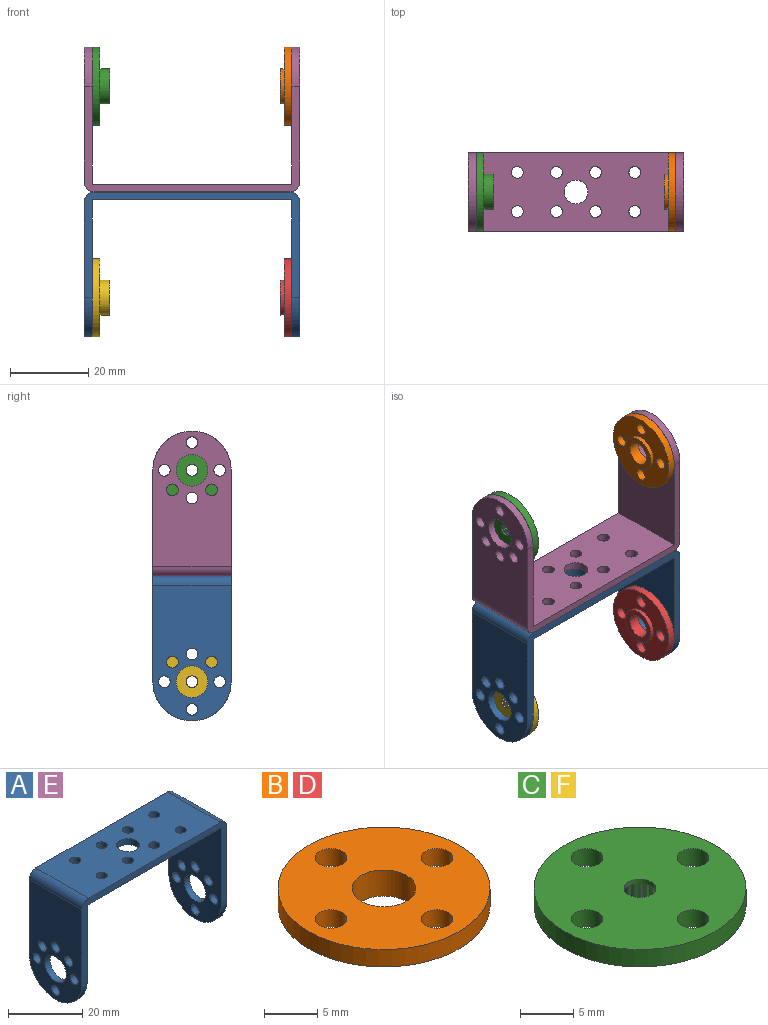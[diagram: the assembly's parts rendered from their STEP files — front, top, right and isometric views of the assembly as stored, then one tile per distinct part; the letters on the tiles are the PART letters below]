
ASSEMBLY  parts=6 mates=5
PART A: 35 faces, bbox 55x20x37 mm
  f0: plane 55x27mm, normal (0,1,0), area 207.3mm2, adj f2,f3,f4,f5,f6,f7,f8,f9
  f1: plane 55x27mm, normal (0,-1,0), area 207.3mm2, adj f2,f3,f4,f5,f6,f7,f8,f9
  f2: plane 35x20mm, normal (-1,0,0), area 563.1mm2, adj f0,f1,f3,f9,f16,f23,f24,f25
  f3: plane 51x20mm, normal (0,0,-1), area 934.2mm2, adj f0,f1,f2,f4,f10,f11,f12,f13
  f4: plane 35x20mm, normal (1,0,0), area 563.1mm2, adj f0,f1,f3,f8,f15,f17,f18,f19
  f5: plane 34.5x20mm, normal (1,0,0), area 553.1mm2, adj f0,f1,f9,f16,f23,f24,f25,f26
  f6: plane 50x20mm, normal (0,0,1), area 914.2mm2, adj f0,f1,f10,f11,f12,f13,f14,f29
  f7: plane 34.5x20mm, normal (-1,0,0), area 553.1mm2, adj f0,f1,f8,f15,f17,f18,f19,f20
  f8: cylinder r=10mm len=20mm, axis (-1,0,0), area 62.8mm2, adj f0,f1,f4,f7
  f9: cylinder r=10mm len=20mm, axis (1,0,0), area 62.8mm2, adj f0,f1,f2,f5
  f10: cylinder r=3.05mm len=6.1mm, axis (0,0,-1), area 38.3mm2, adj f3,f6
  f11: cylinder r=1.5mm len=3mm, axis (0,0,-1), area 18.8mm2, adj f3,f6
  f12: cylinder r=1.5mm len=3mm, axis (0,0,-1), area 18.8mm2, adj f3,f6
  f13: cylinder r=1.5mm len=3mm, axis (0,0,-1), area 18.8mm2, adj f3,f6
  f14: cylinder r=1.5mm len=3mm, axis (0,0,-1), area 18.8mm2, adj f3,f6
  f15: cylinder r=4.05mm len=8.1mm, axis (1,0,0), area 50.9mm2, adj f4,f7
  f16: cylinder r=4.05mm len=8.1mm, axis (1,0,0), area 50.9mm2, adj f2,f5
  f17: cylinder r=1.5mm len=3mm, axis (1,0,0), area 18.8mm2, adj f4,f7
  f18: cylinder r=1.5mm len=3mm, axis (1,0,0), area 18.8mm2, adj f4,f7
  f19: cylinder r=1.5mm len=3mm, axis (1,0,0), area 18.8mm2, adj f4,f7
  f20: cylinder r=1.5mm len=3mm, axis (1,0,0), area 18.8mm2, adj f4,f7
  f21: cylinder r=1.5mm len=3mm, axis (1,0,0), area 18.8mm2, adj f4,f7
  f22: cylinder r=1.5mm len=3mm, axis (1,0,0), area 18.8mm2, adj f4,f7
  f23: cylinder r=1.5mm len=3mm, axis (1,0,0), area 18.8mm2, adj f2,f5
  f24: cylinder r=1.5mm len=3mm, axis (1,0,0), area 18.8mm2, adj f2,f5
  f25: cylinder r=1.5mm len=3mm, axis (1,0,0), area 18.8mm2, adj f2,f5
  f26: cylinder r=1.5mm len=3mm, axis (1,0,0), area 18.8mm2, adj f2,f5
  f27: cylinder r=1.5mm len=3mm, axis (1,0,0), area 18.8mm2, adj f2,f5
  f28: cylinder r=1.5mm len=3mm, axis (1,0,0), area 18.8mm2, adj f2,f5
  f29: cylinder r=2.5mm len=20mm, axis (0,-1,0), area 78.5mm2, adj f0,f1,f5,f6
  f30: cylinder r=2.5mm len=20mm, axis (0,-1,0), area 78.5mm2, adj f0,f1,f6,f7
  f31: cylinder r=1.5mm len=3mm, axis (0,0,-1), area 18.8mm2, adj f3,f6
  f32: cylinder r=1.5mm len=3mm, axis (0,0,-1), area 18.8mm2, adj f3,f6
  f33: cylinder r=1.5mm len=3mm, axis (0,0,-1), area 18.8mm2, adj f3,f6
  f34: cylinder r=1.5mm len=3mm, axis (0,0,-1), area 18.8mm2, adj f3,f6
PART B: 10 faces, bbox 20x20x3 mm
  f0: cylinder r=4.5mm len=9mm, axis (0,0,-1), area 28.3mm2, adj f1,f5
  f1: plane 9x9mm, normal (0,0,-1), area 35.3mm2, adj f0,f2
  f2: cylinder r=3mm len=6mm, axis (0,0,-1), area 56.5mm2, adj f1,f3
  f3: plane 20x20mm, normal (0,0,1), area 257.6mm2, adj f2,f4,f6,f7,f8,f9
  f4: cylinder r=10mm len=20mm, axis (0,0,-1), area 125.7mm2, adj f3,f5
  f5: plane 20x20mm, normal (0,0,-1), area 222.3mm2, adj f0,f4,f6,f7,f8,f9
  f6: cylinder r=1.5mm len=3mm, axis (0,0,-1), area 18.8mm2, adj f3,f5
  f7: cylinder r=1.5mm len=3mm, axis (0,0,-1), area 18.8mm2, adj f3,f5
  f8: cylinder r=1.5mm len=3mm, axis (0,0,-1), area 18.8mm2, adj f3,f5
  f9: cylinder r=1.5mm len=3mm, axis (0,0,-1), area 18.8mm2, adj f3,f5
PART C: 152 faces, bbox 20x20x4.5 mm
  f0: plane 20x20mm, normal (0,0,1), area 278.8mm2, adj f1,f5,f6,f7,f8,f11
  f1: cylinder r=10mm len=20mm, axis (0,0,-1), area 125.7mm2, adj f0,f2
  f2: plane 20x20mm, normal (0,0,-1), area 222.3mm2, adj f1,f3,f5,f6,f7,f8
  f3: cylinder r=4.5mm len=9mm, axis (0,0,-1), area 70.7mm2, adj f2,f4
  f4: plane 9x9mm, normal (0,0,-1), area 35.3mm2, adj f3,f10,f15,f18,f21,f24,f27,f30
  f5: cylinder r=1.5mm len=3mm, axis (0,0,-1), area 18.8mm2, adj f0,f2
  f6: cylinder r=1.5mm len=3mm, axis (0,0,-1), area 18.8mm2, adj f0,f2
  f7: cylinder r=1.5mm len=3mm, axis (0,0,-1), area 18.8mm2, adj f0,f2
  f8: cylinder r=1.5mm len=3mm, axis (0,0,-1), area 18.8mm2, adj f0,f2
  f9: cone r=3mm half-angle=45deg, axis (0,0,-1), area 12.1mm2, adj f10,f12,f13,f14,f15,f16,f17,f18
  f10: cylinder r=3mm len=3.35mm, axis (0,0,-1), area 1mm2, adj f4,f9,f13,f14
  f11: cylinder r=1.5mm len=3mm, axis (0,0,-1), area 4.7mm2, adj f0,f12
  f12: plane 4.7x4.7mm, normal (0,0,-1), area 10.3mm2, adj f9,f11
  f13: plane 3.76x0.42mm, normal (0.23,0.97,0), area 1.4mm2, adj f9,f10,f96,f97
  f14: plane 3.76x0.42mm, normal (0.23,-0.97,0), area 1.4mm2, adj f9,f10,f150,f151
  f15: cylinder r=3mm len=3.35mm, axis (0,0,-1), area 1mm2, adj f4,f9,f16,f17
  f16: plane 3.76x0.39mm, normal (0.45,0.9,0), area 1.4mm2, adj f9,f15,f150,f151
  f17: plane 3.76x0.43mm, normal (0.01,-1,0), area 1.4mm2, adj f9,f15,f148,f149
  f18: cylinder r=3mm len=3.35mm, axis (0,0,-1), area 1mm2, adj f4,f9,f19,f20
  f19: plane 3.76x0.33mm, normal (0.63,0.77,0), area 1.4mm2, adj f9,f18,f148,f149
  f20: plane 3.76x0.42mm, normal (-0.21,-0.98,0), area 1.4mm2, adj f9,f18,f146,f147
  f21: cylinder r=3mm len=3.35mm, axis (0,0,-1), area 1mm2, adj f4,f9,f22,f23
  f22: plane 3.76x0.34mm, normal (0.79,0.61,0), area 1.4mm2, adj f9,f21,f146,f147
  f23: plane 3.76x0.39mm, normal (-0.42,-0.91,0), area 1.4mm2, adj f9,f21,f144,f145
  f24: cylinder r=3mm len=3.35mm, axis (0,0,-1), area 1mm2, adj f4,f9,f25,f26
  f25: plane 3.76x0.39mm, normal (0.91,0.42,0), area 1.4mm2, adj f9,f24,f144,f145
  f26: plane 3.76x0.34mm, normal (-0.61,-0.79,0), area 1.4mm2, adj f9,f24,f142,f143
  f27: cylinder r=3mm len=3.35mm, axis (0,0,-1), area 1mm2, adj f4,f9,f28,f29
  f28: plane 3.76x0.42mm, normal (0.98,0.21,0), area 1.4mm2, adj f9,f27,f142,f143
  f29: plane 3.76x0.33mm, normal (-0.77,-0.63,0), area 1.4mm2, adj f9,f27,f140,f141
  f30: cylinder r=3mm len=3.35mm, axis (0,0,-1), area 1mm2, adj f4,f9,f31,f32
  f31: plane 3.76x0.43mm, normal (1,-0.01,0), area 1.4mm2, adj f9,f30,f140,f141
  f32: plane 3.76x0.39mm, normal (-0.9,-0.45,0), area 1.4mm2, adj f9,f30,f138,f139
  f33: cylinder r=3mm len=3.35mm, axis (0,0,-1), area 1mm2, adj f4,f9,f34,f35
  f34: plane 3.76x0.42mm, normal (0.97,-0.23,0), area 1.4mm2, adj f9,f33,f138,f139
  f35: plane 3.76x0.42mm, normal (-0.97,-0.23,0), area 1.4mm2, adj f9,f33,f136,f137
  f36: cylinder r=3mm len=3.35mm, axis (0,0,-1), area 1mm2, adj f4,f9,f37,f38
  f37: plane 3.76x0.39mm, normal (0.9,-0.45,0), area 1.4mm2, adj f9,f36,f136,f137
  f38: plane 3.76x0.43mm, normal (-1,-0.01,0), area 1.4mm2, adj f9,f36,f134,f135
  f39: cylinder r=3mm len=3.35mm, axis (0,0,-1), area 1mm2, adj f4,f9,f40,f41
  f40: plane 3.76x0.33mm, normal (0.77,-0.63,0), area 1.4mm2, adj f9,f39,f134,f135
  f41: plane 3.76x0.42mm, normal (-0.98,0.21,0), area 1.4mm2, adj f9,f39,f132,f133
  f42: cylinder r=3mm len=3.35mm, axis (0,0,-1), area 1mm2, adj f4,f9,f43,f44
  f43: plane 3.76x0.34mm, normal (0.61,-0.79,0), area 1.4mm2, adj f9,f42,f132,f133
  f44: plane 3.76x0.39mm, normal (-0.91,0.42,0), area 1.4mm2, adj f9,f42,f130,f131
  f45: cylinder r=3mm len=3.35mm, axis (0,0,-1), area 1mm2, adj f4,f9,f46,f47
  f46: plane 3.76x0.39mm, normal (0.42,-0.91,0), area 1.4mm2, adj f9,f45,f130,f131
  f47: plane 3.76x0.34mm, normal (-0.79,0.61,0), area 1.4mm2, adj f9,f45,f128,f129
  f48: cylinder r=3mm len=3.35mm, axis (0,0,-1), area 1mm2, adj f4,f9,f49,f50
  f49: plane 3.76x0.42mm, normal (0.21,-0.98,0), area 1.4mm2, adj f9,f48,f128,f129
  f50: plane 3.76x0.33mm, normal (-0.63,0.77,0), area 1.4mm2, adj f9,f48,f126,f127
  f51: cylinder r=3mm len=3.35mm, axis (0,0,-1), area 1mm2, adj f4,f9,f52,f53
  f52: plane 3.76x0.43mm, normal (-0.01,-1,0), area 1.4mm2, adj f9,f51,f126,f127
  f53: plane 3.76x0.39mm, normal (-0.45,0.9,0), area 1.4mm2, adj f9,f51,f124,f125
  f54: cylinder r=3mm len=3.35mm, axis (0,0,-1), area 1mm2, adj f4,f9,f55,f56
  f55: plane 3.76x0.42mm, normal (-0.23,-0.97,0), area 1.4mm2, adj f9,f54,f124,f125
  f56: plane 3.76x0.42mm, normal (-0.23,0.97,0), area 1.4mm2, adj f9,f54,f122,f123
  f57: cylinder r=3mm len=3.35mm, axis (0,0,-1), area 1mm2, adj f4,f9,f58,f59
  f58: plane 3.76x0.39mm, normal (-0.45,-0.9,0), area 1.4mm2, adj f9,f57,f122,f123
  f59: plane 3.76x0.43mm, normal (-0.01,1,0), area 1.4mm2, adj f9,f57,f120,f121
  f60: cylinder r=3mm len=3.35mm, axis (0,0,-1), area 1mm2, adj f4,f9,f61,f62
  f61: plane 3.76x0.33mm, normal (-0.63,-0.77,0), area 1.4mm2, adj f9,f60,f120,f121
  f62: plane 3.76x0.42mm, normal (0.21,0.98,0), area 1.4mm2, adj f9,f60,f118,f119
  f63: cylinder r=3mm len=3.35mm, axis (0,0,-1), area 1mm2, adj f4,f9,f64,f65
  f64: plane 3.76x0.34mm, normal (-0.79,-0.61,0), area 1.4mm2, adj f9,f63,f118,f119
  f65: plane 3.76x0.39mm, normal (0.42,0.91,0), area 1.4mm2, adj f9,f63,f116,f117
  f66: cylinder r=3mm len=3.35mm, axis (0,0,-1), area 1mm2, adj f4,f9,f67,f68
  f67: plane 3.76x0.39mm, normal (-0.91,-0.42,0), area 1.4mm2, adj f9,f66,f116,f117
  f68: plane 3.76x0.34mm, normal (0.61,0.79,0), area 1.4mm2, adj f9,f66,f114,f115
  f69: cylinder r=3mm len=3.35mm, axis (0,0,-1), area 1mm2, adj f4,f9,f70,f71
  f70: plane 3.76x0.42mm, normal (-0.98,-0.21,0), area 1.4mm2, adj f9,f69,f114,f115
  f71: plane 3.76x0.33mm, normal (0.77,0.63,0), area 1.4mm2, adj f9,f69,f112,f113
  f72: cylinder r=3mm len=3.35mm, axis (0,0,-1), area 1mm2, adj f4,f9,f73,f74
  f73: plane 3.76x0.43mm, normal (-1,0.01,0), area 1.4mm2, adj f9,f72,f112,f113
  f74: plane 3.76x0.39mm, normal (0.9,0.45,0), area 1.4mm2, adj f9,f72,f110,f111
  f75: cylinder r=3mm len=3.35mm, axis (0,0,-1), area 1mm2, adj f4,f9,f76,f77
  f76: plane 3.76x0.42mm, normal (-0.97,0.23,0), area 1.4mm2, adj f9,f75,f110,f111
  f77: plane 3.76x0.42mm, normal (0.97,0.23,0), area 1.4mm2, adj f9,f75,f108,f109
  f78: cylinder r=3mm len=3.35mm, axis (0,0,-1), area 1mm2, adj f4,f9,f79,f80
  f79: plane 3.76x0.39mm, normal (-0.9,0.45,0), area 1.4mm2, adj f9,f78,f108,f109
  f80: plane 3.76x0.43mm, normal (1,0.01,0), area 1.4mm2, adj f9,f78,f106,f107
  f81: cylinder r=3mm len=3.35mm, axis (0,0,-1), area 1mm2, adj f4,f9,f82,f83
  f82: plane 3.76x0.33mm, normal (-0.77,0.63,0), area 1.4mm2, adj f9,f81,f106,f107
  f83: plane 3.76x0.42mm, normal (0.98,-0.21,0), area 1.4mm2, adj f9,f81,f104,f105
  f84: cylinder r=3mm len=3.35mm, axis (0,0,-1), area 1mm2, adj f4,f9,f85,f86
  f85: plane 3.76x0.34mm, normal (-0.61,0.79,0), area 1.4mm2, adj f9,f84,f104,f105
  f86: plane 3.76x0.39mm, normal (0.91,-0.42,0), area 1.4mm2, adj f9,f84,f102,f103
  f87: cylinder r=3mm len=3.35mm, axis (0,0,-1), area 1mm2, adj f4,f9,f88,f89
  f88: plane 3.76x0.39mm, normal (-0.42,0.91,0), area 1.4mm2, adj f9,f87,f102,f103
  f89: plane 3.76x0.34mm, normal (0.79,-0.61,0), area 1.4mm2, adj f9,f87,f100,f101
  f90: cylinder r=3mm len=3.35mm, axis (0,0,-1), area 1mm2, adj f4,f9,f91,f92
  f91: plane 3.76x0.42mm, normal (-0.21,0.98,0), area 1.4mm2, adj f9,f90,f100,f101
  f92: plane 3.76x0.33mm, normal (0.63,-0.77,0), area 1.4mm2, adj f9,f90,f98,f99
  f93: cylinder r=3mm len=3.35mm, axis (0,0,-1), area 1mm2, adj f4,f9,f94,f95
  f94: plane 3.76x0.43mm, normal (0.01,1,0), area 1.4mm2, adj f9,f93,f98,f99
  f95: plane 3.76x0.39mm, normal (0.45,-0.9,0), area 1.4mm2, adj f9,f93,f96,f97
  f96: cone r=2.6mm half-angle=60deg, axis (0,0,-1), area 0.1mm2, adj f4,f13,f95,f97
  f97: cylinder r=2.6mm len=3.52mm, axis (0,0,-1), area 0.3mm2, adj f9,f13,f95,f96
  f98: cone r=2.6mm half-angle=60deg, axis (0,0,-1), area 0.1mm2, adj f4,f92,f94,f99
  f99: cylinder r=2.6mm len=3.52mm, axis (0,0,-1), area 0.3mm2, adj f9,f92,f94,f98
  f100: cone r=2.6mm half-angle=60deg, axis (0,0,-1), area 0.1mm2, adj f4,f89,f91,f101
  f101: cylinder r=2.6mm len=3.52mm, axis (0,0,-1), area 0.3mm2, adj f9,f89,f91,f100
  f102: cone r=2.6mm half-angle=60deg, axis (0,0,-1), area 0.1mm2, adj f4,f86,f88,f103
  f103: cylinder r=2.6mm len=3.52mm, axis (0,0,-1), area 0.3mm2, adj f9,f86,f88,f102
  f104: cone r=2.6mm half-angle=60deg, axis (0,0,-1), area 0.1mm2, adj f4,f83,f85,f105
  f105: cylinder r=2.6mm len=3.52mm, axis (0,0,-1), area 0.3mm2, adj f9,f83,f85,f104
  f106: cone r=2.6mm half-angle=60deg, axis (0,0,-1), area 0.1mm2, adj f4,f80,f82,f107
  f107: cylinder r=2.6mm len=3.52mm, axis (0,0,-1), area 0.3mm2, adj f9,f80,f82,f106
  f108: cone r=2.6mm half-angle=60deg, axis (0,0,-1), area 0.1mm2, adj f4,f77,f79,f109
  f109: cylinder r=2.6mm len=3.52mm, axis (0,0,-1), area 0.3mm2, adj f9,f77,f79,f108
  f110: cone r=2.6mm half-angle=60deg, axis (0,0,-1), area 0.1mm2, adj f4,f74,f76,f111
  f111: cylinder r=2.6mm len=3.52mm, axis (0,0,-1), area 0.3mm2, adj f9,f74,f76,f110
  f112: cone r=2.6mm half-angle=60deg, axis (0,0,-1), area 0.1mm2, adj f4,f71,f73,f113
  f113: cylinder r=2.6mm len=3.52mm, axis (0,0,-1), area 0.3mm2, adj f9,f71,f73,f112
  f114: cone r=2.6mm half-angle=60deg, axis (0,0,-1), area 0.1mm2, adj f4,f68,f70,f115
  f115: cylinder r=2.6mm len=3.52mm, axis (0,0,-1), area 0.3mm2, adj f9,f68,f70,f114
  f116: cone r=2.6mm half-angle=60deg, axis (0,0,-1), area 0.1mm2, adj f4,f65,f67,f117
  f117: cylinder r=2.6mm len=3.52mm, axis (0,0,-1), area 0.3mm2, adj f9,f65,f67,f116
  f118: cone r=2.6mm half-angle=60deg, axis (0,0,-1), area 0.1mm2, adj f4,f62,f64,f119
  f119: cylinder r=2.6mm len=3.52mm, axis (0,0,-1), area 0.3mm2, adj f9,f62,f64,f118
  f120: cone r=2.6mm half-angle=60deg, axis (0,0,-1), area 0.1mm2, adj f4,f59,f61,f121
  f121: cylinder r=2.6mm len=3.52mm, axis (0,0,-1), area 0.3mm2, adj f9,f59,f61,f120
  f122: cone r=2.6mm half-angle=60deg, axis (0,0,-1), area 0.1mm2, adj f4,f56,f58,f123
  f123: cylinder r=2.6mm len=3.52mm, axis (0,0,-1), area 0.3mm2, adj f9,f56,f58,f122
  f124: cone r=2.6mm half-angle=60deg, axis (0,0,-1), area 0.1mm2, adj f4,f53,f55,f125
  f125: cylinder r=2.6mm len=3.52mm, axis (0,0,-1), area 0.3mm2, adj f9,f53,f55,f124
  f126: cone r=2.6mm half-angle=60deg, axis (0,0,-1), area 0.1mm2, adj f4,f50,f52,f127
  f127: cylinder r=2.6mm len=3.52mm, axis (0,0,-1), area 0.3mm2, adj f9,f50,f52,f126
  f128: cone r=2.6mm half-angle=60deg, axis (0,0,-1), area 0.1mm2, adj f4,f47,f49,f129
  f129: cylinder r=2.6mm len=3.52mm, axis (0,0,-1), area 0.3mm2, adj f9,f47,f49,f128
  f130: cone r=2.6mm half-angle=60deg, axis (0,0,-1), area 0.1mm2, adj f4,f44,f46,f131
  f131: cylinder r=2.6mm len=3.52mm, axis (0,0,-1), area 0.3mm2, adj f9,f44,f46,f130
  f132: cone r=2.6mm half-angle=60deg, axis (0,0,-1), area 0.1mm2, adj f4,f41,f43,f133
  f133: cylinder r=2.6mm len=3.52mm, axis (0,0,-1), area 0.3mm2, adj f9,f41,f43,f132
  f134: cone r=2.6mm half-angle=60deg, axis (0,0,-1), area 0.1mm2, adj f4,f38,f40,f135
  f135: cylinder r=2.6mm len=3.52mm, axis (0,0,-1), area 0.3mm2, adj f9,f38,f40,f134
  f136: cone r=2.6mm half-angle=60deg, axis (0,0,-1), area 0.1mm2, adj f4,f35,f37,f137
  f137: cylinder r=2.6mm len=3.52mm, axis (0,0,-1), area 0.3mm2, adj f9,f35,f37,f136
  f138: cone r=2.6mm half-angle=60deg, axis (0,0,-1), area 0.1mm2, adj f4,f32,f34,f139
  f139: cylinder r=2.6mm len=3.52mm, axis (0,0,-1), area 0.3mm2, adj f9,f32,f34,f138
  f140: cone r=2.6mm half-angle=60deg, axis (0,0,-1), area 0.1mm2, adj f4,f29,f31,f141
  f141: cylinder r=2.6mm len=3.52mm, axis (0,0,-1), area 0.3mm2, adj f9,f29,f31,f140
  f142: cone r=2.6mm half-angle=60deg, axis (0,0,-1), area 0.1mm2, adj f4,f26,f28,f143
  f143: cylinder r=2.6mm len=3.52mm, axis (0,0,-1), area 0.3mm2, adj f9,f26,f28,f142
  f144: cone r=2.6mm half-angle=60deg, axis (0,0,-1), area 0.1mm2, adj f4,f23,f25,f145
  f145: cylinder r=2.6mm len=3.52mm, axis (0,0,-1), area 0.3mm2, adj f9,f23,f25,f144
  f146: cone r=2.6mm half-angle=60deg, axis (0,0,-1), area 0.1mm2, adj f4,f20,f22,f147
  f147: cylinder r=2.6mm len=3.52mm, axis (0,0,-1), area 0.3mm2, adj f9,f20,f22,f146
  f148: cone r=2.6mm half-angle=60deg, axis (0,0,-1), area 0.1mm2, adj f4,f17,f19,f149
  f149: cylinder r=2.6mm len=3.52mm, axis (0,0,-1), area 0.3mm2, adj f9,f17,f19,f148
  f150: cylinder r=2.6mm len=3.52mm, axis (0,0,-1), area 0.3mm2, adj f9,f14,f16,f151
  f151: cone r=2.6mm half-angle=60deg, axis (0,0,-1), area 0.1mm2, adj f4,f14,f16,f150
PART D: same geometry as B
PART E: same geometry as A
PART F: same geometry as C
PLACE A t=(0,0,-37)mm
PLACE B rot(axis=(0,1,0),90deg) t=(5.5,0,27)mm
PLACE C rot(axis=(0,-1,0),90deg) t=(-21,0,27)mm
PLACE D rot(axis=(0,1,0),90deg) t=(5.5,0,-27)mm
PLACE E rot(axis=(1,0,0),180deg) t=(0,0,37)mm
PLACE F rot(axis=(0,-1,0),90deg) t=(-21,0,-27)mm
MATE fastened E.f15 <-> C.f1  axis (1,0,0) through (-25.5,0,27)mm
MATE fastened A.f10 <-> E.f10  axis (0,0,1) through (0,0,0)mm
MATE fastened A.f8 <-> F.f1  axis (1,0,0) through (-25.5,0,-27)mm
MATE fastened E.f15 <-> B.f0  axis (-1,0,0) through (25.5,0,27)mm
MATE fastened D.f0 <-> A.f9  axis (1,0,0) through (25.5,0,-27)mm
